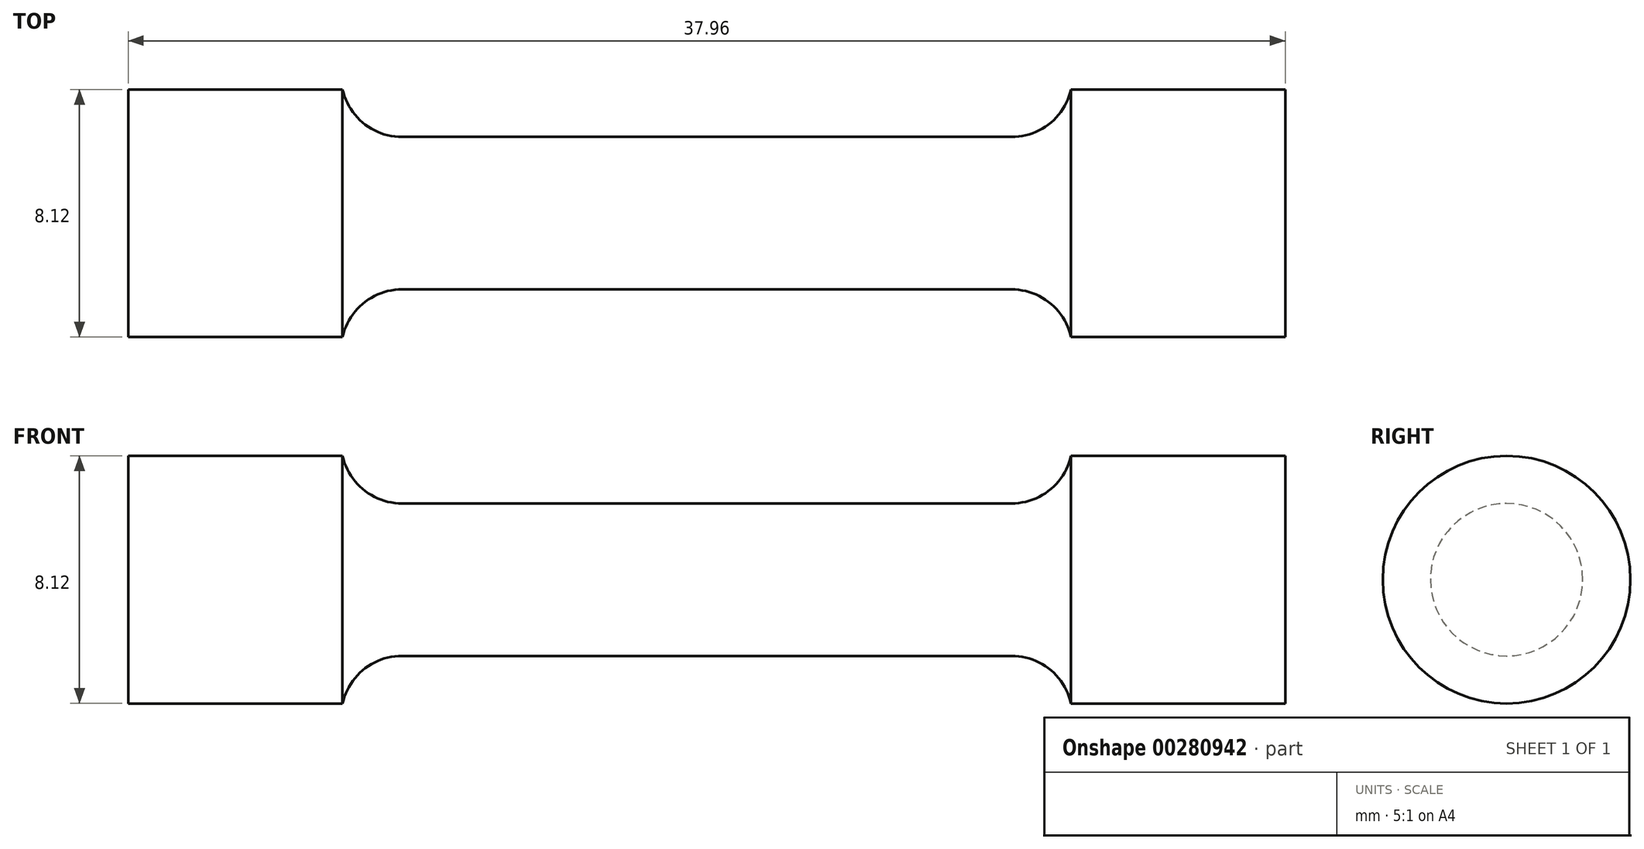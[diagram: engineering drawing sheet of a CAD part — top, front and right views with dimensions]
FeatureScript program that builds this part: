
annotation { "Feature Type Name" : "Feature", "Feature Type Description" : "" }
export const myFeature = defineFeature(function(context is Context, id is Id, definition is map)
    precondition{}
    {
        {
            var Q0;
            Q0=qCreatedBy(makeId("Front.planeOp"),FACE);
            var sketch = newSketch(context, id + "F0", { "sketchPlane" : qUnion([Q0])});
            skLineSegment(sketch, "E0", {"start": v(0, 2.5) * mm, "end": v(10, 2.5) * mm});
            skArc(sketch, "E1", {"start": v(10, 2.5) * mm, "mid": v(11.25, 2.94) * mm, "end": v(11.95, 4.06) * mm});
            skLineSegment(sketch, "E2", {"start": v(11.95, 4.06) * mm, "end": v(18.98, 4.06) * mm});
            skLineSegment(sketch, "E3", {"start": v(18.98, 0) * mm, "end": v(18.98, 4.06) * mm});
            skLineSegment(sketch, "E4", {"start": v(18.98, 0) * mm, "end": v(0, 0) * mm});
            skLineSegment(sketch, "E5.MirrorCS", {"start": v(0, 2.5) * mm, "end": v(-10, 2.5) * mm});
            skLineSegment(sketch, "E6.MirrorCS", {"start": v(-18.98, 0) * mm, "end": v(0, 0) * mm});
            skLineSegment(sketch, "E7.MirrorCS", {"start": v(-11.95, 4.06) * mm, "end": v(-18.98, 4.06) * mm});
            skLineSegment(sketch, "E8.MirrorCS", {"start": v(-18.98, 0) * mm, "end": v(-18.98, 4.06) * mm});
            skArc(sketch, "E9.MirrorCS", {"start": v(-10, 2.5) * mm, "mid": v(-11.25, 2.94) * mm, "end": v(-11.95, 4.06) * mm});
            skSolve(sketch);
        }
        {
            var Q0;
            Q0=makeQuery(id+"F0.imprint","IMPRINT",FACE,{"disambiguationData":[TD([[makeQuery(id+"F0.imprint","IMPRINT",EDGE,{"derivedFrom":sQuery(id+"F0.wireOp",EDGE,"E0")}),-1.0]])]});
            var Q1;
            Q1=sQuery(id+"F0.wireOp",EDGE,"E6.MirrorCS");
            revolve(context, id + "F1", {"entities" : qUnion([Q0]), "axis" : qUnion([Q1]), "revolveType" : RevolveType.FULL});
        }
    });
